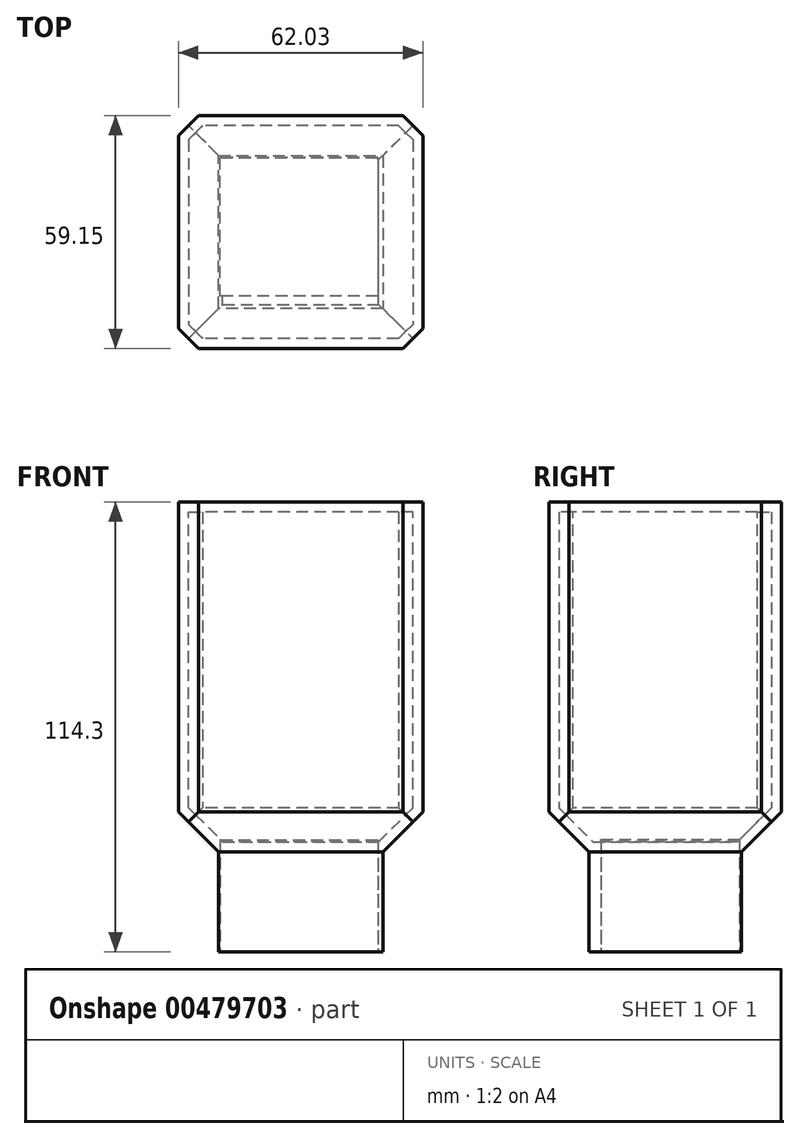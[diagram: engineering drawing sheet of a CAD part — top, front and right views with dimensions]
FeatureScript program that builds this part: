
annotation { "Feature Type Name" : "Feature", "Feature Type Description" : "" }
export const myFeature = defineFeature(function(context is Context, id is Id, definition is map)
    precondition{}
    {
        {
            var Q0;
            Q0=qCreatedBy(makeId("Top.planeOp"),FACE);
            var sketch = newSketch(context, id + "F0", { "sketchPlane" : qUnion([Q0])});
            skLineSegment(sketch, "E0.bottom", {"start": v(31.09, 28.53) * mm, "end": v(-30.94, 28.53) * mm});
            skLineSegment(sketch, "E0.top", {"start": v(31.09, -30.62) * mm, "end": v(-30.94, -30.62) * mm});
            skLineSegment(sketch, "E0.left", {"start": v(31.09, 28.53) * mm, "end": v(31.09, -30.62) * mm});
            skLineSegment(sketch, "E0.right", {"start": v(-30.94, 28.53) * mm, "end": v(-30.94, -30.62) * mm});
            skSolve(sketch);
        }
        {
            var Q0;
            Q0=makeQuery(id+"F0.imprint","IMPRINT",FACE,{"disambiguationData":[TD([[makeQuery(id+"F0.imprint","IMPRINT",EDGE,{"derivedFrom":sQuery(id+"F0.wireOp",EDGE,"E0.bottom")}),1.0]])]});
            extrude(context, id + "F1", {"entities" : qUnion([Q0]), "oppositeDirection" : true, "depth" : 88.9 * mm});
        }
        {
            var Q0;
            Q0=makeQuery(id+"F1.opExtrude","CAP_FACE",FACE,{"disambiguationData":[OSD([sQuery(id+"F0.wireOp",EDGE,"E0.bottom"),sQuery(id+"F0.wireOp",EDGE,"E0.top"),sQuery(id+"F0.wireOp",EDGE,"E0.left"),sQuery(id+"F0.wireOp",EDGE,"E0.right")])],"isStart":false});
            var sketch = newSketch(context, id + "F2", { "sketchPlane" : qUnion([Q0])});
            skLineSegment(sketch, "E1.bottom", {"start": v(-20.4, 17.32) * mm, "end": v(19.67, 17.32) * mm});
            skLineSegment(sketch, "E1.top", {"start": v(-20.4, -17.86) * mm, "end": v(19.67, -17.86) * mm});
            skLineSegment(sketch, "E1.left", {"start": v(-20.4, 17.32) * mm, "end": v(-20.4, -17.86) * mm});
            skLineSegment(sketch, "E1.right", {"start": v(19.67, 17.32) * mm, "end": v(19.67, -17.86) * mm});
            skSolve(sketch);
        }
        {
            var Q0;
            Q0=makeQuery(id+"F2.imprint","IMPRINT",FACE,{"disambiguationData":[TD([[makeQuery(id+"F2.imprint","IMPRINT",EDGE,{"derivedFrom":sQuery(id+"F2.wireOp",EDGE,"E1.bottom")}),-1.0]])]});
            extrude(context, id + "F3", {"entities" : qUnion([Q0]), "operationType" : NewBodyOperationType.REMOVE, "endBound" : BoundingType.SYMMETRIC, "oppositeDirection" : true, "depth" : 152.4 * mm});
        }
        {
            var Q0;
            Q0=makeQuery(id+"F1.opExtrude","SWEPT_EDGE",EDGE,{"disambiguationData":[OSD([sQuery(id+"F0.wireOp",EDGE,"E0.bottom"),sQuery(id+"F0.wireOp",EDGE,"E0.right")])]});
            var Q1;
            Q1=makeQuery(id+"F1.opExtrude","SWEPT_EDGE",EDGE,{"disambiguationData":[OSD([sQuery(id+"F0.wireOp",EDGE,"E0.bottom"),sQuery(id+"F0.wireOp",EDGE,"E0.left")])]});
            var Q2;
            Q2=makeQuery(id+"F1.opExtrude","SWEPT_EDGE",EDGE,{"disambiguationData":[OSD([sQuery(id+"F0.wireOp",EDGE,"E0.top"),sQuery(id+"F0.wireOp",EDGE,"E0.left")])]});
            var Q3;
            Q3=makeQuery(id+"F1.opExtrude","SWEPT_EDGE",EDGE,{"disambiguationData":[OSD([sQuery(id+"F0.wireOp",EDGE,"E0.top"),sQuery(id+"F0.wireOp",EDGE,"E0.right")])]});
            chamfer(context, id + "F4", {"entities" : qUnion([Q0, Q1, Q2, Q3]), "width" : 5.08 * mm, "tangentPropagation" : true});
        }
        {
            var Q0;
            Q0=makeQuery(id+"F1.opExtrude","CAP_EDGE",EDGE,{"disambiguationData":[OSD([sQuery(id+"F0.wireOp",EDGE,"E0.top")])],"isStart":false});
            var Q1;
            Q1=makeQuery(id+"F1.opExtrude","CAP_EDGE",EDGE,{"disambiguationData":[OSD([sQuery(id+"F0.wireOp",EDGE,"E0.bottom")])],"isStart":false});
            var Q2;
            Q2=makeQuery(id+"F1.opExtrude","CAP_EDGE",EDGE,{"disambiguationData":[OSD([sQuery(id+"F0.wireOp",EDGE,"E0.left")])],"isStart":false});
            var Q3;
            Q3=makeQuery(id+"F1.opExtrude","CAP_EDGE",EDGE,{"disambiguationData":[OSD([sQuery(id+"F0.wireOp",EDGE,"E0.right")])],"isStart":false});
            chamfer(context, id + "F5", {"entities" : qUnion([Q0, Q1, Q2, Q3]), "width" : 10.16 * mm, "tangentPropagation" : true});
        }
        {
            var Q0;
            Q0=makeQuery(id+"F3.boolean.opBoolean","COPY",FACE,{"derivedFrom":makeQuery(id+"F3.opExtrude","SWEPT_FACE",FACE,{"disambiguationData":[OSD([sQuery(id+"F2.wireOp",EDGE,"E1.top")])]})});
            var Q1;
            Q1=makeQuery(id+"F3.boolean.opBoolean","COPY",FACE,{"derivedFrom":makeQuery(id+"F3.opExtrude","SWEPT_FACE",FACE,{"disambiguationData":[OSD([sQuery(id+"F2.wireOp",EDGE,"E1.right")])]})});
            var Q2;
            Q2=makeQuery(id+"F3.boolean.opBoolean","COPY",FACE,{"derivedFrom":makeQuery(id+"F3.opExtrude","SWEPT_FACE",FACE,{"disambiguationData":[OSD([sQuery(id+"F2.wireOp",EDGE,"E1.left")])]})});
            var Q3;
            Q3=makeQuery(id+"F3.boolean.opBoolean","COPY",FACE,{"derivedFrom":makeQuery(id+"F3.opExtrude","SWEPT_FACE",FACE,{"disambiguationData":[OSD([sQuery(id+"F2.wireOp",EDGE,"E1.bottom")])]})});
            var Q4;
            Q4=makeQuery(id+"F3.boolean.opBoolean","COPY",FACE,{"derivedFrom":makeQuery(id+"F3.opExtrude","CAP_FACE",FACE,{"disambiguationData":[OSD([sQuery(id+"F2.wireOp",EDGE,"E1.bottom"),sQuery(id+"F2.wireOp",EDGE,"E1.top"),sQuery(id+"F2.wireOp",EDGE,"E1.left"),sQuery(id+"F2.wireOp",EDGE,"E1.right")])],"isStart":false})});
            shell(context, id + "F6", {"entities" : qUnion([Q0, Q1, Q2, Q3, Q4]), "thickness" : 2.54 * mm});
        }
        {
            var Q0;
            Q0=makeQuery(id+"F1.opExtrude","CAP_FACE",FACE,{"disambiguationData":[OSD([sQuery(id+"F0.wireOp",EDGE,"E0.bottom"),sQuery(id+"F0.wireOp",EDGE,"E0.top"),sQuery(id+"F0.wireOp",EDGE,"E0.left"),sQuery(id+"F0.wireOp",EDGE,"E0.right")])],"isStart":false});
            extrude(context, id + "F7", {"entities" : qUnion([Q0]), "operationType" : NewBodyOperationType.ADD, "depth" : 25.4 * mm});
        }
    });
